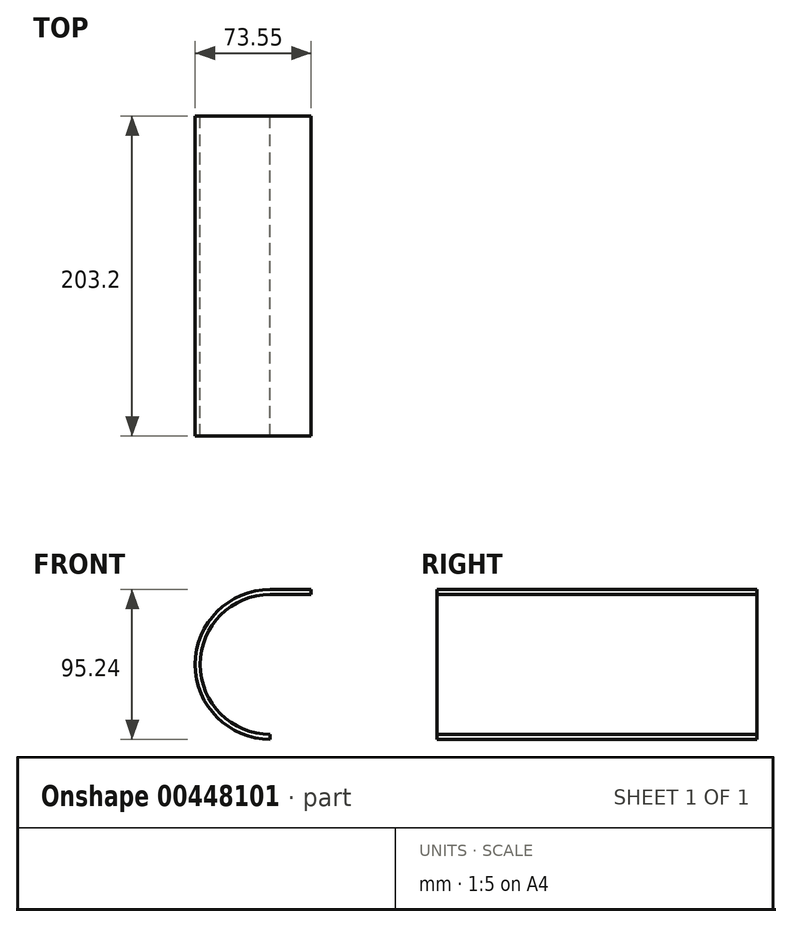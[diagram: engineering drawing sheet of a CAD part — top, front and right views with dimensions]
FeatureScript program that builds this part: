
annotation { "Feature Type Name" : "Feature", "Feature Type Description" : "" }
export const myFeature = defineFeature(function(context is Context, id is Id, definition is map)
    precondition{}
    {
        {
            var Q0;
            Q0=qCreatedBy(makeId("Front.planeOp"),FACE);
            var sketch = newSketch(context, id + "F0", { "sketchPlane" : qUnion([Q0])});
            skArc(sketch, "E0", {"start": v(0, 44.45) * mm, "mid": v(-44.45, 0) * mm, "end": v(0, -44.45) * mm});
            skLineSegment(sketch, "E1", {"start": v(0, 44.45) * mm, "end": v(0, -44.45) * mm, "construction": true});
            skPoint(sketch, "E2.orphan", {"position": v(0, 128) * mm});
            skArc(sketch, "E3.0", {"start": v(0, 47.62) * mm, "mid": v(-47.62, 0) * mm, "end": v(0, -47.62) * mm});
            skLineSegment(sketch, "E4", {"start": v(0, -44.45) * mm, "end": v(0, -47.62) * mm});
            skLineSegment(sketch, "E5", {"start": v(0, 47.62) * mm, "end": v(25.93, 47.62) * mm});
            skLineSegment(sketch, "E6", {"start": v(25.93, 47.62) * mm, "end": v(25.93, 44.45) * mm});
            skLineSegment(sketch, "E7", {"start": v(25.93, 44.45) * mm, "end": v(0, 44.45) * mm});
            skSolve(sketch);
        }
        {
            var Q0;
            Q0=makeQuery(id+"F0.imprint","IMPRINT",FACE,{"disambiguationData":[TD([[makeQuery(id+"F0.imprint","IMPRINT",EDGE,{"derivedFrom":sQuery(id+"F0.wireOp",EDGE,"E0")}),-1.0]])]});
            extrude(context, id + "F1", {"entities" : qUnion([Q0]), "depth" : 203.2 * mm});
        }
        {
            var Q0;
            Q0 = qSketchRegion(id + "F0", true);
            extrude(context, id + "F2", {"entities" : qUnion([Q0]), "operationType" : NewBodyOperationType.ADD, "depth" : 25.4 * mm});
        }
    });
